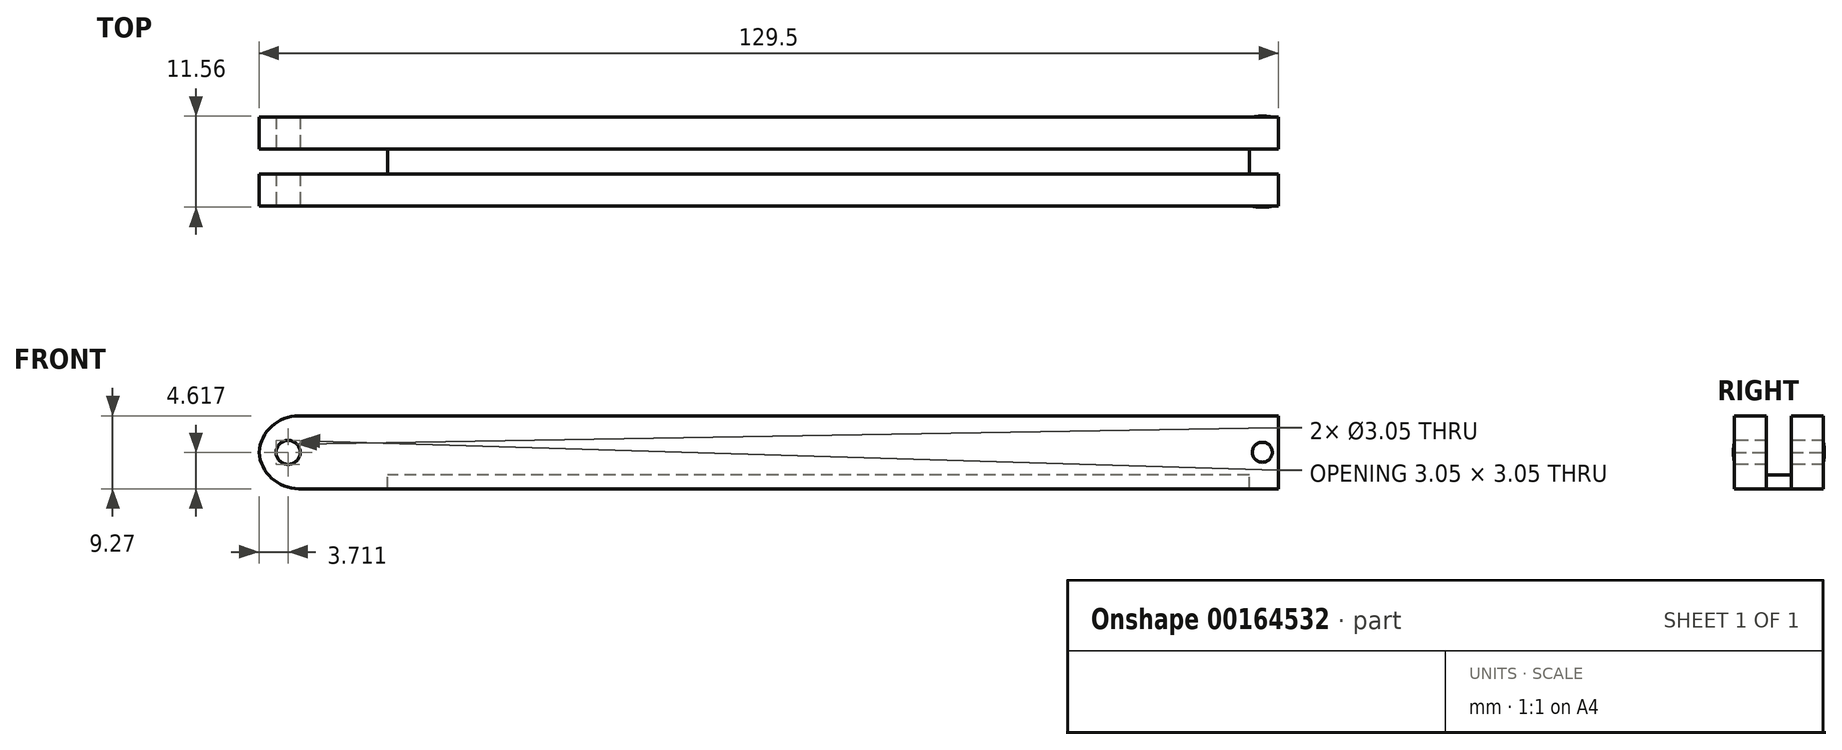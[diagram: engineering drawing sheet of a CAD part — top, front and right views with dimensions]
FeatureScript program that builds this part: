
annotation { "Feature Type Name" : "Feature", "Feature Type Description" : "" }
export const myFeature = defineFeature(function(context is Context, id is Id, definition is map)
    precondition{}
    {
        {
            var Q0;
            Q0=qCreatedBy(makeId("Top.planeOp"),FACE);
            var sketch = newSketch(context, id + "F0", { "sketchPlane" : qUnion([Q0])});
            skLineSegment(sketch, "E0.bottom", {"start": v(64.76, 5.65) * mm, "end": v(-64.76, 5.65) * mm});
            skLineSegment(sketch, "E0.top", {"start": v(64.76, -5.65) * mm, "end": v(-64.76, -5.65) * mm});
            skLineSegment(sketch, "E0.left", {"start": v(64.76, 5.65) * mm, "end": v(64.76, -5.65) * mm});
            skLineSegment(sketch, "E0.right", {"start": v(-64.76, 5.65) * mm, "end": v(-64.76, -5.65) * mm});
            skPoint(sketch, "E0.middle", {"position": v(0, 0) * mm});
            skSolve(sketch);
        }
        {
            var Q0;
            Q0 = qSketchRegion(id + "F0", true);
            extrude(context, id + "F1", {"entities" : qUnion([Q0]), "depth" : 9.27 * mm});
        }
        {
            var Q0;
            Q0=makeQuery(id+"F1.opExtrude","CAP_FACE",FACE,{"disambiguationData":[OSD([sQuery(id+"F0.wireOp",EDGE,"E0.bottom"),sQuery(id+"F0.wireOp",EDGE,"E0.top"),sQuery(id+"F0.wireOp",EDGE,"E0.left"),sQuery(id+"F0.wireOp",EDGE,"E0.right")])],"isStart":false});
            var sketch = newSketch(context, id + "F2", { "sketchPlane" : qUnion([Q0])});
            skLineSegment(sketch, "E1.bottom", {"start": v(103.18, -1.59) * mm, "end": v(-103.18, -1.59) * mm});
            skLineSegment(sketch, "E1.top", {"start": v(103.18, 1.59) * mm, "end": v(-103.18, 1.59) * mm});
            skLineSegment(sketch, "E1.left", {"start": v(103.18, -1.59) * mm, "end": v(103.18, 1.59) * mm});
            skLineSegment(sketch, "E1.right", {"start": v(-103.18, -1.59) * mm, "end": v(-103.18, 1.59) * mm});
            skPoint(sketch, "E1.middle", {"position": v(0, 0) * mm});
            skSolve(sketch);
        }
        {
            var Q0;
            Q0 = qSketchRegion(id + "F2", true);
            extrude(context, id + "F3", {"entities" : qUnion([Q0]), "operationType" : NewBodyOperationType.REMOVE, "oppositeDirection" : true, "depth" : 7.54 * mm});
        }
        {
            var Q0;
            Q0=makeQuery(id+"F3.boolean.opBoolean","COPY",FACE,{"derivedFrom":makeQuery(id+"F3.opExtrude","CAP_FACE",FACE,{"disambiguationData":[OSD([sQuery(id+"F2.wireOp",EDGE,"E1.bottom"),sQuery(id+"F2.wireOp",EDGE,"E1.top"),sQuery(id+"F2.wireOp",EDGE,"E1.left"),sQuery(id+"F2.wireOp",EDGE,"E1.right")])],"isStart":false})});
            var sketch = newSketch(context, id + "F4", { "sketchPlane" : qUnion([Q0])});
            skLineSegment(sketch, "E2.bottom", {"start": v(64.76, 1.59) * mm, "end": v(61.05, 1.59) * mm});
            skLineSegment(sketch, "E2.top", {"start": v(64.76, -1.59) * mm, "end": v(61.05, -1.59) * mm});
            skLineSegment(sketch, "E2.left", {"start": v(64.76, 1.59) * mm, "end": v(64.76, -1.59) * mm});
            skLineSegment(sketch, "E2.right", {"start": v(61.05, 1.59) * mm, "end": v(61.05, -1.59) * mm});
            skSolve(sketch);
        }
        {
            var Q0;
            Q0 = qSketchRegion(id + "F4", true);
            extrude(context, id + "F5", {"entities" : qUnion([Q0]), "operationType" : NewBodyOperationType.REMOVE, "oppositeDirection" : true, "depth" : 25.4 * mm});
        }
        {
            var Q0;
            Q0=makeQuery(id+"F3.boolean.opBoolean","COPY",FACE,{"derivedFrom":makeQuery(id+"F3.opExtrude","CAP_FACE",FACE,{"disambiguationData":[OSD([sQuery(id+"F2.wireOp",EDGE,"E1.bottom"),sQuery(id+"F2.wireOp",EDGE,"E1.top"),sQuery(id+"F2.wireOp",EDGE,"E1.left"),sQuery(id+"F2.wireOp",EDGE,"E1.right")])],"isStart":false})});
            var sketch = newSketch(context, id + "F6", { "sketchPlane" : qUnion([Q0])});
            skLineSegment(sketch, "E3.bottom", {"start": v(-64.76, 1.59) * mm, "end": v(-48.43, 1.59) * mm});
            skLineSegment(sketch, "E3.top", {"start": v(-64.76, -1.59) * mm, "end": v(-48.43, -1.59) * mm});
            skLineSegment(sketch, "E3.left", {"start": v(-64.76, 1.59) * mm, "end": v(-64.76, -1.59) * mm});
            skLineSegment(sketch, "E3.right", {"start": v(-48.43, 1.59) * mm, "end": v(-48.43, -1.59) * mm});
            skSolve(sketch);
        }
        {
            var Q0;
            Q0 = qSketchRegion(id + "F6", true);
            extrude(context, id + "F7", {"entities" : qUnion([Q0]), "operationType" : NewBodyOperationType.REMOVE, "oppositeDirection" : true, "depth" : 25.4 * mm});
        }
        {
            var Q0;
            {var subQ0=sQuery(id+"F0.wireOp",EDGE,"E0.right");var subQ1=sQuery(id+"F0.wireOp",EDGE,"E0.top");Q0=makeQuery(id+"F3.boolean.opBoolean","SPLIT",EDGE,{"disambiguationData":[TD([makeQuery(id+"F1.opExtrude","SWEPT_FACE",FACE,{"disambiguationData":[OSD([subQ1])]})])],"derivedFrom":makeQuery(id+"F1.opExtrude","CAP_EDGE",EDGE,{"disambiguationData":[OSD([subQ0])],"isStart":false})});}
            var Q1;
            {var subQ0=sQuery(id+"F0.wireOp",EDGE,"E0.right");var subQ1=sQuery(id+"F0.wireOp",EDGE,"E0.top");Q1=makeQuery(id+"F7.boolean.opBoolean","SPLIT",EDGE,{"disambiguationData":[TD([makeQuery(id+"F1.opExtrude","SWEPT_FACE",FACE,{"disambiguationData":[OSD([subQ1])]})])],"derivedFrom":makeQuery(id+"F1.opExtrude","CAP_EDGE",EDGE,{"disambiguationData":[OSD([subQ0])],"isStart":true})});}
            var Q2;
            {var subQ0=sQuery(id+"F0.wireOp",EDGE,"E0.bottom");var subQ1=sQuery(id+"F0.wireOp",EDGE,"E0.right");Q2=makeQuery(id+"F3.boolean.opBoolean","SPLIT",EDGE,{"disambiguationData":[TD([makeQuery(id+"F1.opExtrude","SWEPT_FACE",FACE,{"disambiguationData":[OSD([subQ0])]})])],"derivedFrom":makeQuery(id+"F1.opExtrude","CAP_EDGE",EDGE,{"disambiguationData":[OSD([subQ1])],"isStart":false})});}
            var Q3;
            {var subQ0=sQuery(id+"F0.wireOp",EDGE,"E0.right");var subQ1=sQuery(id+"F0.wireOp",EDGE,"E0.bottom");Q3=makeQuery(id+"F7.boolean.opBoolean","SPLIT",EDGE,{"disambiguationData":[TD([makeQuery(id+"F1.opExtrude","SWEPT_FACE",FACE,{"disambiguationData":[OSD([subQ1])]})])],"derivedFrom":makeQuery(id+"F1.opExtrude","CAP_EDGE",EDGE,{"disambiguationData":[OSD([subQ0])],"isStart":true})});}
            fillet(context, id + "F8", {"entities" : qUnion([Q0, Q1, Q2, Q3]), "radius" : 5.08 * mm, "tangentPropagation" : true, "allowEdgeOverflow" : false});
        }
        {
            var Q0;
            Q0=makeQuery(id+"F1.opExtrude","SWEPT_FACE",FACE,{"disambiguationData":[OSD([sQuery(id+"F0.wireOp",EDGE,"E0.top")])]});
            var sketch = newSketch(context, id + "F9", { "sketchPlane" : qUnion([Q0])});
            skCircle(sketch, "E4", {"center": v(-61.03, 4.62) * mm, "radius": 1.52 * mm});
            skSolve(sketch);
        }
        {
            var Q0;
            Q0 = qSketchRegion(id + "F9", true);
            extrude(context, id + "F10", {"entities" : qUnion([Q0]), "operationType" : NewBodyOperationType.REMOVE, "oppositeDirection" : true, "depth" : 25.4 * mm});
        }
        {
            var Q0;
            Q0=makeQuery(id+"F1.opExtrude","SWEPT_FACE",FACE,{"disambiguationData":[OSD([sQuery(id+"F0.wireOp",EDGE,"E0.top")])]});
            var sketch = newSketch(context, id + "F11", { "sketchPlane" : qUnion([Q0])});
            skCircle(sketch, "E5", {"center": v(62.73, 4.64) * mm, "radius": 1.27 * mm});
            skLineSegment(sketch, "E6", {"start": v(64.76, 4.64) * mm, "end": v(41.42, 4.64) * mm});
            skSolve(sketch);
        }
        {
            var Q0;
            Q0 = qSketchRegion(id + "F11", true);
            extrude(context, id + "F12", {"entities" : qUnion([Q0]), "operationType" : NewBodyOperationType.ADD, "depth" : 0.13 * mm});
        }
        {
            var Q0;
            Q0=makeQuery(id+"F12.opExtrude","CAP_FACE",FACE,{"disambiguationData":[OSD([sQuery(id+"F11.wireOp",EDGE,"E5")])],"isStart":false});
            fillet(context, id + "F13", {"entities" : qUnion([Q0]), "radius" : 5.08 * mm, "tangentPropagation" : true, "allowEdgeOverflow" : false});
        }
        {
            var Q0;
            Q0=makeQuery(id+"F1.opExtrude","SWEPT_BODY",BODY,{"disambiguationData":[OSD([sQuery(id+"F0.wireOp",EDGE,"E0.bottom"),sQuery(id+"F0.wireOp",EDGE,"E0.top"),sQuery(id+"F0.wireOp",EDGE,"E0.left"),sQuery(id+"F0.wireOp",EDGE,"E0.right")])]});
            var Q1;
            Q1=qCreatedBy(makeId("Front.planeOp"),FACE);
            mirror(context, id + "F14", {"operationType" : NewBodyOperationType.ADD, "entities" : qUnion([Q0]), "mirrorPlane" : qUnion([Q1])});
        }
    });
